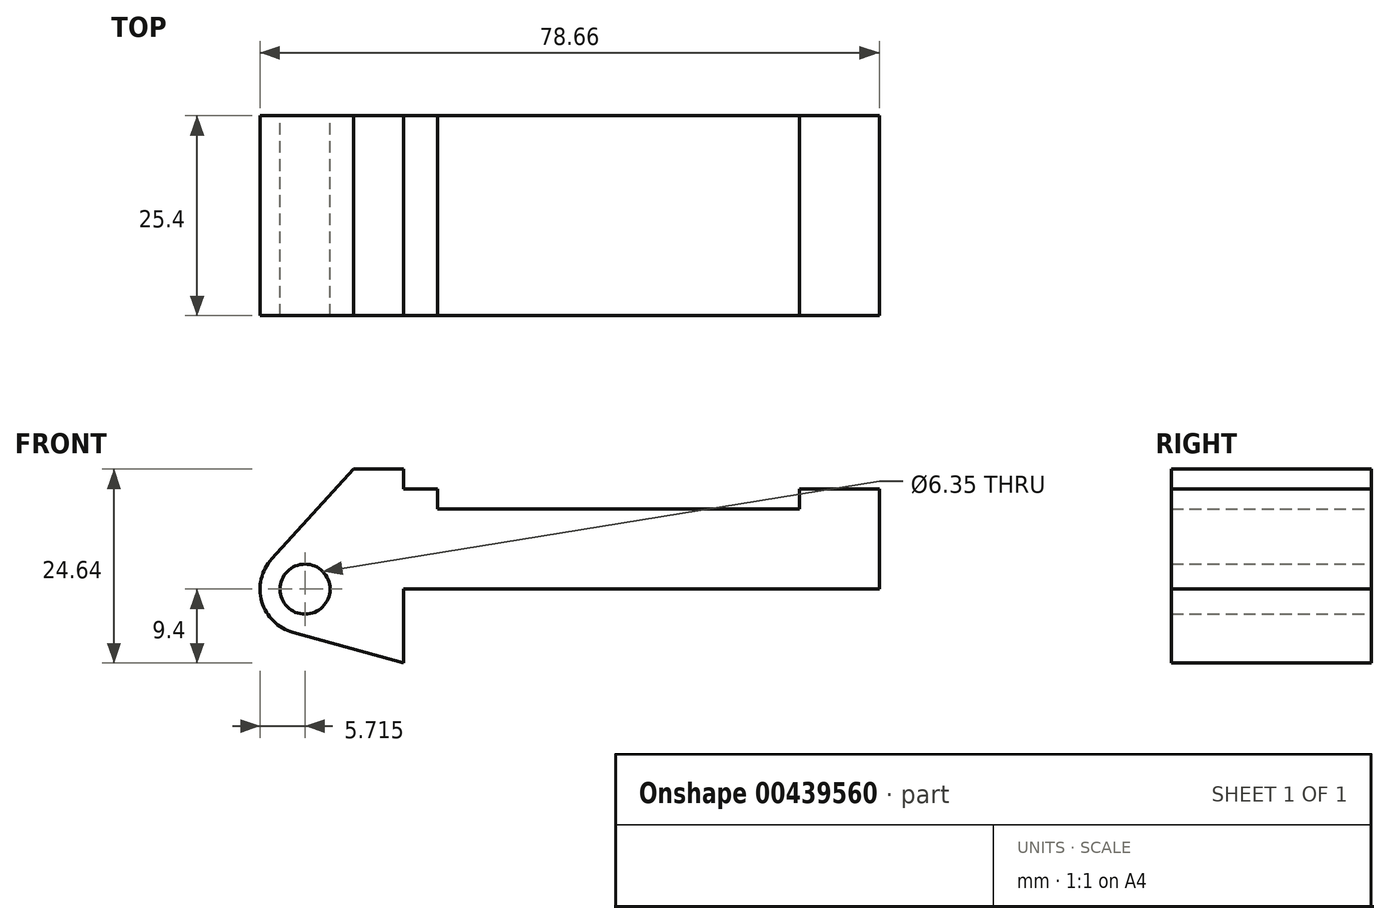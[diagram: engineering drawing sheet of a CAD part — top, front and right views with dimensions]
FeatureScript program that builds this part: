
annotation { "Feature Type Name" : "Feature", "Feature Type Description" : "" }
export const myFeature = defineFeature(function(context is Context, id is Id, definition is map)
    precondition{}
    {
        {
            var Q0;
            Q0=qCreatedBy(makeId("Front.planeOp"),FACE);
            var sketch = newSketch(context, id + "F0", { "sketchPlane" : qUnion([Q0])});
            skLineSegment(sketch, "E0", {"start": v(0, 0) * mm, "end": v(0, 12.7) * mm});
            skLineSegment(sketch, "E1", {"start": v(0, 12.7) * mm, "end": v(10.16, 12.7) * mm});
            skLineSegment(sketch, "E2", {"start": v(10.16, 12.7) * mm, "end": v(10.16, 10.16) * mm});
            skLineSegment(sketch, "E3", {"start": v(10.16, 10.16) * mm, "end": v(56.13, 10.16) * mm});
            skLineSegment(sketch, "E4", {"start": v(56.13, 10.16) * mm, "end": v(56.13, 12.7) * mm});
            skLineSegment(sketch, "E5", {"start": v(56.13, 12.7) * mm, "end": v(66.3, 12.7) * mm});
            skLineSegment(sketch, "E6", {"start": v(66.3, 12.7) * mm, "end": v(66.3, 0) * mm});
            skLineSegment(sketch, "E7", {"start": v(66.3, 0) * mm, "end": v(0, 0) * mm});
            skLineSegment(sketch, "E8", {"start": v(5.84, 15.24) * mm, "end": v(-0.5, 15.24) * mm});
            skLineSegment(sketch, "E9", {"start": v(-0.5, 15.24) * mm, "end": v(-10.88, 3.85) * mm});
            skLineSegment(sketch, "E10", {"start": v(0, 0) * mm, "end": v(-6.65, 0) * mm});
            skCircle(sketch, "E11", {"center": v(-6.65, 0) * mm, "radius": 5.72 * mm});
            skCircle(sketch, "E12", {"center": v(-6.65, 0) * mm, "radius": 3.18 * mm});
            skLineSegment(sketch, "E13", {"start": v(5.84, 15.24) * mm, "end": v(5.84, -9.4) * mm});
            skLineSegment(sketch, "E14", {"start": v(5.84, -9.4) * mm, "end": v(-8.18, -5.5) * mm});
            skSolve(sketch);
        }
        {
            var Q0;
            {var subQ0=sQuery(id+"F0.wireOp",EDGE,"E2");Q0=makeQuery(id+"F0.imprint","IMPRINT",FACE,{"disambiguationData":[TD([[makeQuery(id+"F0.imprint","IMPRINT",EDGE,{"derivedFrom":subQ0}),-1.0]])]});}
            var Q1;
            {var subQ0=sQuery(id+"F0.wireOp",EDGE,"E0");Q1=makeQuery(id+"F0.imprint","IMPRINT",FACE,{"disambiguationData":[TD([[makeQuery(id+"F0.imprint","IMPRINT",EDGE,{"derivedFrom":subQ0}),-1.0]])]});}
            var Q2;
            {var subQ1=sQuery(id+"F0.wireOp",EDGE,"E0");Q2=makeQuery(id+"F0.imprint","IMPRINT",FACE,{"disambiguationData":[TD([[makeQuery(id+"F0.imprint","IMPRINT",EDGE,{"derivedFrom":subQ1}),1.0]])]});}
            var Q3;
            {var subQ0=sQuery(id+"F0.wireOp",EDGE,"E14");Q3=makeQuery(id+"F0.imprint","IMPRINT",FACE,{"disambiguationData":[TD([[makeQuery(id+"F0.imprint","IMPRINT",EDGE,{"derivedFrom":subQ0}),-1.0]])]});}
            var Q4;
            {var subQ5=sQuery(id+"F0.wireOp",EDGE,"E12");Q4=makeQuery(id+"F0.imprint","IMPRINT",FACE,{"disambiguationData":[TD([[makeQuery(id+"F0.imprint","IMPRINT",EDGE,{"derivedFrom":subQ5}),-1.0]])]});}
            extrude(context, id + "F1", {"entities" : qUnion([Q0, Q1, Q2, Q3, Q4]), "depth" : 25.4 * mm});
        }
    });
